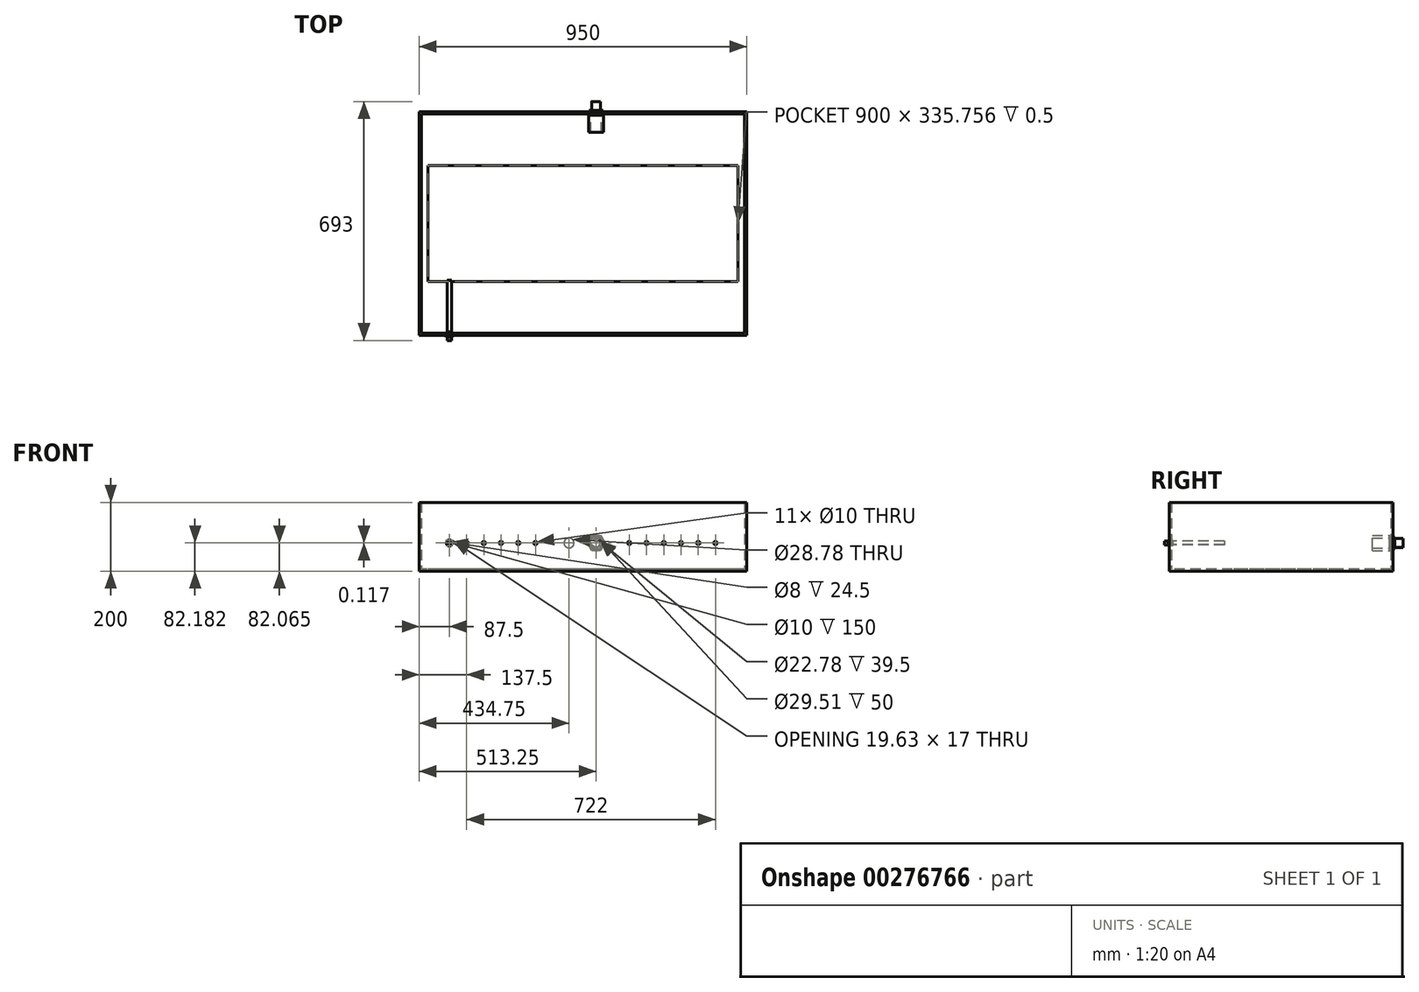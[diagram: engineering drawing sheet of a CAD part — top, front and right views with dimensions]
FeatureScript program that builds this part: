
annotation { "Feature Type Name" : "Feature", "Feature Type Description" : "" }
export const myFeature = defineFeature(function(context is Context, id is Id, definition is map)
    precondition{}
    {
        {
            var Q0;
            Q0=qCreatedBy(makeId("Top.planeOp"),FACE);
            var sketch = newSketch(context, id + "F0", { "sketchPlane" : qUnion([Q0])});
            skLineSegment(sketch, "E0.bottom", {"start": v(475, 325) * mm, "end": v(-475, 325) * mm});
            skLineSegment(sketch, "E0.top", {"start": v(475, -325) * mm, "end": v(-475, -325) * mm});
            skLineSegment(sketch, "E0.left", {"start": v(475, 325) * mm, "end": v(475, -325) * mm});
            skLineSegment(sketch, "E0.right", {"start": v(-475, 325) * mm, "end": v(-475, -325) * mm});
            skPoint(sketch, "E0.middle", {"position": v(0, 0) * mm});
            skSolve(sketch);
        }
        {
            var Q0;
            Q0=makeQuery(id+"F0.imprint","IMPRINT",FACE,{"disambiguationData":[TD([[makeQuery(id+"F0.imprint","IMPRINT",EDGE,{"derivedFrom":sQuery(id+"F0.wireOp",EDGE,"cca13281-c8a4-43dd-b4c7-58c42d9eb948.0")}),1.0]])]});
            var Q1;
            Q1=makeQuery(id+"F0.imprint","IMPRINT",FACE,{"disambiguationData":[TD([[makeQuery(id+"F0.imprint","IMPRINT",EDGE,{"derivedFrom":sQuery(id+"F0.wireOp",EDGE,"E0.bottom")}),1.0]])]});
            extrude(context, id + "F1", {"entities" : qUnion([Q0, Q1]), "depth" : 200 * mm});
        }
        {
            var Q0;
            Q0=makeQuery(id+"F1.opExtrude","CAP_FACE",FACE,{"disambiguationData":[OSD([sQuery(id+"F0.wireOp",EDGE,"E0.bottom"),sQuery(id+"F0.wireOp",EDGE,"E0.top"),sQuery(id+"F0.wireOp",EDGE,"E0.left"),sQuery(id+"F0.wireOp",EDGE,"E0.right")])],"isStart":false});
            shell(context, id + "F2", {"entities" : qUnion([Q0]), "thickness" : 2.5 * mm});
        }
        {
            var Q0;
            Q0=makeQuery(id+"F2.opShell","OFFSET_FACE",FACE,{"disambiguationData":[OSD([sQuery(id+"F0.wireOp",EDGE,"E0.bottom"),sQuery(id+"F0.wireOp",EDGE,"E0.top"),sQuery(id+"F0.wireOp",EDGE,"E0.left"),sQuery(id+"F0.wireOp",EDGE,"E0.right")])]});
            extrude(context, id + "F3", {"entities" : qUnion([Q0]), "depth" : 197.5 * mm});
        }
        {
            var Q0;
            Q0=makeQuery(id+"F3.opExtrude","CAP_FACE",FACE,{"disambiguationData":[OSD([sQuery(id+"F0.wireOp",EDGE,"E0.bottom"),sQuery(id+"F0.wireOp",EDGE,"E0.top"),sQuery(id+"F0.wireOp",EDGE,"E0.left"),sQuery(id+"F0.wireOp",EDGE,"E0.right")])],"isStart":false});
            shell(context, id + "F4", {"entities" : qUnion([Q0]), "thickness" : 4 * mm});
        }
        {
            var Q0;
            Q0=makeQuery(id+"F4.opShell","OFFSET_FACE",FACE,{"disambiguationData":[OSD([sQuery(id+"F0.wireOp",EDGE,"E0.bottom"),sQuery(id+"F0.wireOp",EDGE,"E0.top"),sQuery(id+"F0.wireOp",EDGE,"E0.left"),sQuery(id+"F0.wireOp",EDGE,"E0.right")])]});
            var sketch = newSketch(context, id + "F5", { "sketchPlane" : qUnion([Q0])});
            skLineSegment(sketch, "E1.bottom", {"start": v(450, 167.88) * mm, "end": v(-450, 167.88) * mm});
            skLineSegment(sketch, "E1.top", {"start": v(450, -167.88) * mm, "end": v(-450, -167.88) * mm});
            skLineSegment(sketch, "E1.left", {"start": v(450, 167.88) * mm, "end": v(450, -167.88) * mm});
            skLineSegment(sketch, "E1.right", {"start": v(-450, 167.88) * mm, "end": v(-450, -167.88) * mm});
            skPoint(sketch, "E1.middle", {"position": v(0, 0) * mm});
            skLineSegment(sketch, "E2.bottom", {"start": v(468.5, 318.5) * mm, "end": v(-468.5, 318.5) * mm});
            skLineSegment(sketch, "E2.top", {"start": v(468.5, -318.5) * mm, "end": v(-468.5, -318.5) * mm});
            skLineSegment(sketch, "E2.left", {"start": v(468.5, 318.5) * mm, "end": v(468.5, -318.5) * mm});
            skLineSegment(sketch, "E2.right", {"start": v(-468.5, 318.5) * mm, "end": v(-468.5, -318.5) * mm});
            skSolve(sketch);
        }
        {
            var Q0;
            Q0=makeQuery(id+"F5.imprint","IMPRINT",FACE,{"disambiguationData":[TD([[makeQuery(id+"F5.imprint","IMPRINT",EDGE,{"derivedFrom":sQuery(id+"F5.wireOp",EDGE,"E1.bottom")}),-1.0]])]});
            extrude(context, id + "F6", {"entities" : qUnion([Q0]), "operationType" : NewBodyOperationType.ADD, "depth" : 0.5 * mm});
        }
        {
            var Q0;
            Q0=makeQuery(id+"F1.opExtrude","SWEPT_FACE",FACE,{"disambiguationData":[OSD([sQuery(id+"F0.wireOp",EDGE,"E0.top")])]});
            var sketch = newSketch(context, id + "F7", { "sketchPlane" : qUnion([Q0])});
            skLineSegment(sketch, "E3.top", {"start": v(450, 6.5) * mm, "end": v(-450, 6.5) * mm, "construction": true});
            skPoint(sketch, "E3.middle", {"position": v(0, 100) * mm});
            skPoint(sketch, "E3.middle.positionSnap0", {"position": v(-475, 100) * mm});
            skPoint(sketch, "E3.centerSnap0", {"position": v(-475, 100) * mm});
            skLineSegment(sketch, "E4", {"start": v(-450, 6.5) * mm, "end": v(-450, 251.45) * mm, "construction": true});
            skLineSegment(sketch, "E5", {"start": v(-450, 251.45) * mm, "end": v(450, 251.45) * mm, "construction": true});
            skLineSegment(sketch, "E6", {"start": v(450, 251.45) * mm, "end": v(450, 6.5) * mm, "construction": true});
            skLineSegment(sketch, "E7", {"start": v(-450, 82.18) * mm, "end": v(-387.5, 82.18) * mm, "construction": true});
            skLineSegment(sketch, "E8", {"start": v(-387.5, 82.18) * mm, "end": v(-387.5, 6.5) * mm, "construction": true});
            skCircle(sketch, "E9", {"center": v(-387.5, 82.18) * mm, "radius": 5 * mm});
            skCircle(sketch, "E10.1.0.0", {"center": v(-337.5, 82.18) * mm, "radius": 5 * mm});
            skCircle(sketch, "E10.2.0.0", {"center": v(-287.5, 82.18) * mm, "radius": 5 * mm});
            skCircle(sketch, "E10.3.0.0", {"center": v(-237.5, 82.18) * mm, "radius": 5 * mm});
            skCircle(sketch, "E10.4.0.0", {"center": v(-187.5, 82.18) * mm, "radius": 5 * mm});
            skCircle(sketch, "E10.5.0.0", {"center": v(-137.5, 82.18) * mm, "radius": 5 * mm});
            skLineSegment(sketch, "E10.direction1", {"start": v(-387.5, 82.18) * mm, "end": v(-337.5, 82.18) * mm, "construction": true});
            skLineSegment(sketch, "E11", {"start": v(450, 82.07) * mm, "end": v(384.5, 82.07) * mm, "construction": true});
            skLineSegment(sketch, "E12", {"start": v(384.5, 82.07) * mm, "end": v(384.5, 6.5) * mm, "construction": true});
            skCircle(sketch, "E13", {"center": v(384.5, 82.07) * mm, "radius": 5 * mm});
            skCircle(sketch, "E14.1.0.0", {"center": v(334.5, 82.07) * mm, "radius": 5 * mm});
            skCircle(sketch, "E14.2.0.0", {"center": v(284.5, 82.07) * mm, "radius": 5 * mm});
            skCircle(sketch, "E14.3.0.0", {"center": v(234.5, 82.07) * mm, "radius": 5 * mm});
            skCircle(sketch, "E14.4.0.0", {"center": v(184.5, 82.07) * mm, "radius": 5 * mm});
            skCircle(sketch, "E14.5.0.0", {"center": v(134.5, 82.07) * mm, "radius": 5 * mm});
            skLineSegment(sketch, "E14.direction1", {"start": v(384.5, 82.07) * mm, "end": v(334.5, 82.07) * mm, "construction": true});
            skSolve(sketch);
        }
        {
            var Q0;
            Q0 = qSketchRegion(id + "F7", true);
            extrude(context, id + "F8", {"entities" : qUnion([Q0]), "operationType" : NewBodyOperationType.REMOVE, "oppositeDirection" : true, "depth" : 25 * mm});
        }
        {
            var Q0;
            Q0=makeQuery(id+"F1.opExtrude","SWEPT_FACE",FACE,{"disambiguationData":[OSD([sQuery(id+"F0.wireOp",EDGE,"E0.bottom")])]});
            var sketch = newSketch(context, id + "F9", { "sketchPlane" : qUnion([Q0])});
            skLineSegment(sketch, "E15", {"start": v(-450, 251.45) * mm, "end": v(-450, 6.5) * mm, "construction": true});
            skLineSegment(sketch, "E16", {"start": v(-450, 6.5) * mm, "end": v(450, 6.5) * mm, "construction": true});
            skLineSegment(sketch, "E17", {"start": v(450, 6.5) * mm, "end": v(450, 251.45) * mm, "construction": true});
            skLineSegment(sketch, "E18", {"start": v(450, 251.45) * mm, "end": v(-450, 251.45) * mm, "construction": true});
            skLineSegment(sketch, "E19", {"start": v(40.25, 6.5) * mm, "end": v(40.25, 82.07) * mm, "construction": true});
            skLineSegment(sketch, "E20", {"start": v(40.25, 82.07) * mm, "end": v(450, 82.07) * mm, "construction": true});
            skCircle(sketch, "E21", {"center": v(40.25, 82.07) * mm, "radius": 14.39 * mm});
            skCircle(sketch, "E22.1.0.0", {"center": v(-38.25, 82.07) * mm, "radius": 14.39 * mm});
            skLineSegment(sketch, "E22.direction1", {"start": v(40.25, 82.07) * mm, "end": v(-38.25, 82.07) * mm, "construction": true});
            skSolve(sketch);
        }
        {
            var Q0;
            Q0 = qSketchRegion(id + "F9", true);
            extrude(context, id + "F10", {"entities" : qUnion([Q0]), "operationType" : NewBodyOperationType.REMOVE, "oppositeDirection" : true, "depth" : 15 * mm});
        }
        {
            var Q0;
            Q0=makeQuery(id+"F1.opExtrude","SWEPT_FACE",FACE,{"disambiguationData":[OSD([sQuery(id+"F0.wireOp",EDGE,"E0.top")])]});
            var sketch = newSketch(context, id + "F11", { "sketchPlane" : qUnion([Q0])});
            skCircle(sketch, "E23", {"center": v(-387.5, 82.18) * mm, "radius": 4 * mm});
            skCircle(sketch, "E24.cCircle", {"center": v(-387.5, 82.18) * mm, "radius": 8.5 * mm, "construction": true});
            skLineSegment(sketch, "E24.0", {"start": v(-392.4, 90.68) * mm, "end": v(-382.6, 90.68) * mm});
            skLineSegment(sketch, "E24.1", {"start": v(-382.6, 90.68) * mm, "end": v(-377.69, 82.18) * mm});
            skLineSegment(sketch, "E24.2", {"start": v(-377.69, 82.18) * mm, "end": v(-382.6, 73.68) * mm});
            skLineSegment(sketch, "E24.3", {"start": v(-382.6, 73.68) * mm, "end": v(-392.4, 73.68) * mm});
            skLineSegment(sketch, "E24.4", {"start": v(-392.4, 73.68) * mm, "end": v(-397.31, 82.18) * mm});
            skLineSegment(sketch, "E24.5", {"start": v(-397.31, 82.18) * mm, "end": v(-392.4, 90.68) * mm});
            skPoint(sketch, "E24.0.midPoint", {"position": v(-387.5, 90.68) * mm});
            skSolve(sketch);
        }
        {
            var Q0;
            Q0 = qSketchRegion(id + "F11", true);
            extrude(context, id + "F12", {"entities" : qUnion([Q0]), "depth" : 4 * mm});
        }
        {
            var Q0;
            Q0=makeQuery(id+"F12.opExtrude","CAP_FACE",FACE,{"disambiguationData":[OSD([sQuery(id+"F11.wireOp",EDGE,"E23"),sQuery(id+"F11.wireOp",EDGE,"E24.0"),sQuery(id+"F11.wireOp",EDGE,"E24.1"),sQuery(id+"F11.wireOp",EDGE,"E24.2"),sQuery(id+"F11.wireOp",EDGE,"E24.3"),sQuery(id+"F11.wireOp",EDGE,"E24.4"),sQuery(id+"F11.wireOp",EDGE,"E24.5")])],"isStart":false});
            var sketch = newSketch(context, id + "F13", { "sketchPlane" : qUnion([Q0])});
            skCircle(sketch, "E25", {"center": v(-387.5, 82.18) * mm, "radius": 6 * mm});
            skCircle(sketch, "E26", {"center": v(-387.5, 82.18) * mm, "radius": 4 * mm});
            skSolve(sketch);
        }
        {
            var Q0;
            Q0 = qSketchRegion(id + "F13", true);
            extrude(context, id + "F14", {"entities" : qUnion([Q0]), "operationType" : NewBodyOperationType.ADD, "depth" : 10 * mm});
        }
        {
            var Q0;
            Q0=makeQuery(id+"F12.opExtrude","CAP_FACE",FACE,{"disambiguationData":[OSD([sQuery(id+"F11.wireOp",EDGE,"E23"),sQuery(id+"F11.wireOp",EDGE,"E24.0"),sQuery(id+"F11.wireOp",EDGE,"E24.1"),sQuery(id+"F11.wireOp",EDGE,"E24.2"),sQuery(id+"F11.wireOp",EDGE,"E24.3"),sQuery(id+"F11.wireOp",EDGE,"E24.4"),sQuery(id+"F11.wireOp",EDGE,"E24.5")])],"isStart":true});
            var sketch = newSketch(context, id + "F15", { "sketchPlane" : qUnion([Q0])});
            skCircle(sketch, "E27", {"center": v(387.5, 82.18) * mm, "radius": 5 * mm});
            skCircle(sketch, "E28", {"center": v(387.5, 82.18) * mm, "radius": 4 * mm});
            skSolve(sketch);
        }
        {
            var Q0;
            Q0 = qSketchRegion(id + "F15", true);
            extrude(context, id + "F16", {"entities" : qUnion([Q0]), "operationType" : NewBodyOperationType.ADD, "depth" : 6.5 * mm});
        }
        {
            var Q0;
            Q0=makeQuery(id+"F16.opExtrude","CAP_FACE",FACE,{"disambiguationData":[OSD([sQuery(id+"F15.wireOp",EDGE,"E27"),sQuery(id+"F15.wireOp",EDGE,"E28")])],"isStart":false});
            var sketch = newSketch(context, id + "F17", { "sketchPlane" : qUnion([Q0])});
            skCircle(sketch, "E29.cCircle", {"center": v(387.5, 82.18) * mm, "radius": 8.5 * mm, "construction": true});
            skLineSegment(sketch, "E29.0", {"start": v(382.6, 90.68) * mm, "end": v(392.4, 90.68) * mm});
            skLineSegment(sketch, "E29.1", {"start": v(392.4, 90.68) * mm, "end": v(397.31, 82.18) * mm});
            skLineSegment(sketch, "E29.2", {"start": v(397.31, 82.18) * mm, "end": v(392.4, 73.68) * mm});
            skLineSegment(sketch, "E29.3", {"start": v(392.4, 73.68) * mm, "end": v(382.6, 73.68) * mm});
            skLineSegment(sketch, "E29.4", {"start": v(382.6, 73.68) * mm, "end": v(377.69, 82.18) * mm});
            skLineSegment(sketch, "E29.5", {"start": v(377.69, 82.18) * mm, "end": v(382.6, 90.68) * mm});
            skPoint(sketch, "E29.0.midPoint", {"position": v(387.5, 90.68) * mm});
            skCircle(sketch, "E30", {"center": v(387.5, 82.18) * mm, "radius": 4 * mm});
            skSolve(sketch);
        }
        {
            var Q0;
            Q0=makeQuery(id+"F17.imprint","IMPRINT",FACE,{"disambiguationData":[TD([[makeQuery(id+"F17.imprint","IMPRINT",EDGE,{"derivedFrom":sQuery(id+"F17.wireOp",EDGE,"E30")}),1.0]])]});
            var Q1;
            Q1=makeQuery(id+"F17.imprint","IMPRINT",FACE,{"disambiguationData":[TD([[makeQuery(id+"F17.imprint","IMPRINT",EDGE,{"derivedFrom":sQuery(id+"F17.wireOp",EDGE,"E29.0")}),-1.0]])]});
            extrude(context, id + "F18", {"entities" : qUnion([Q0, Q1]), "operationType" : NewBodyOperationType.ADD, "depth" : 4 * mm});
        }
        {
            var Q0;
            Q0=makeQuery(id+"F18.opExtrude","CAP_FACE",FACE,{"disambiguationData":[OSD([sQuery(id+"F17.wireOp",EDGE,"E29.0"),sQuery(id+"F17.wireOp",EDGE,"E29.1"),sQuery(id+"F17.wireOp",EDGE,"E29.2"),sQuery(id+"F17.wireOp",EDGE,"E29.3"),sQuery(id+"F17.wireOp",EDGE,"E29.4"),sQuery(id+"F17.wireOp",EDGE,"E29.5"),sQuery(id+"F17.wireOp",EDGE,"E30")])],"isStart":false});
            var sketch = newSketch(context, id + "F19", { "sketchPlane" : qUnion([Q0])});
            skCircle(sketch, "E31", {"center": v(387.5, 82.18) * mm, "radius": 6 * mm});
            skCircle(sketch, "E32", {"center": v(387.5, 82.18) * mm, "radius": 5 * mm});
            skSolve(sketch);
        }
        {
            var Q0;
            Q0 = qSketchRegion(id + "F19", true);
            extrude(context, id + "F20", {"entities" : qUnion([Q0]), "operationType" : NewBodyOperationType.ADD, "depth" : 150 * mm});
        }
        {
            var Q0;
            Q0=makeQuery(id+"F1.opExtrude","SWEPT_FACE",FACE,{"disambiguationData":[OSD([sQuery(id+"F0.wireOp",EDGE,"E0.bottom")])]});
            var sketch = newSketch(context, id + "F21", { "sketchPlane" : qUnion([Q0])});
            skCircle(sketch, "E33", {"center": v(-38.25, 82.07) * mm, "radius": 11.39 * mm});
            skCircle(sketch, "E34.cCircle", {"center": v(-38.25, 82.07) * mm, "radius": 17.48 * mm, "construction": true});
            skLineSegment(sketch, "E34.0", {"start": v(-48.34, 99.55) * mm, "end": v(-28.16, 99.55) * mm});
            skLineSegment(sketch, "E34.1", {"start": v(-28.16, 99.55) * mm, "end": v(-18.07, 82.07) * mm});
            skLineSegment(sketch, "E34.2", {"start": v(-18.07, 82.07) * mm, "end": v(-28.16, 64.58) * mm});
            skLineSegment(sketch, "E34.3", {"start": v(-28.16, 64.58) * mm, "end": v(-48.34, 64.58) * mm});
            skLineSegment(sketch, "E34.4", {"start": v(-48.34, 64.58) * mm, "end": v(-58.43, 82.06) * mm});
            skLineSegment(sketch, "E34.5", {"start": v(-58.43, 82.06) * mm, "end": v(-48.34, 99.55) * mm});
            skPoint(sketch, "E34.0.midPoint", {"position": v(-38.25, 99.55) * mm});
            skSolve(sketch);
        }
        {
            var Q0;
            Q0 = qSketchRegion(id + "F21", true);
            extrude(context, id + "F22", {"entities" : qUnion([Q0]), "depth" : 4 * mm});
        }
        {
            var Q0;
            Q0=makeQuery(id+"F22.opExtrude","CAP_FACE",FACE,{"disambiguationData":[OSD([sQuery(id+"F21.wireOp",EDGE,"E33"),sQuery(id+"F21.wireOp",EDGE,"E34.0"),sQuery(id+"F21.wireOp",EDGE,"E34.1"),sQuery(id+"F21.wireOp",EDGE,"E34.2"),sQuery(id+"F21.wireOp",EDGE,"E34.3"),sQuery(id+"F21.wireOp",EDGE,"E34.4"),sQuery(id+"F21.wireOp",EDGE,"E34.5")])],"isStart":false});
            var sketch = newSketch(context, id + "F23", { "sketchPlane" : qUnion([Q0])});
            skCircle(sketch, "E35", {"center": v(-38.25, 82.07) * mm, "radius": 13.03 * mm});
            skCircle(sketch, "E36", {"center": v(-38.25, 82.07) * mm, "radius": 11.39 * mm});
            skSolve(sketch);
        }
        {
            var Q0;
            Q0 = qSketchRegion(id + "F23", true);
            extrude(context, id + "F24", {"entities" : qUnion([Q0]), "operationType" : NewBodyOperationType.ADD, "depth" : 25 * mm});
        }
        {
            var Q0;
            Q0=makeQuery(id+"F22.opExtrude","CAP_FACE",FACE,{"disambiguationData":[OSD([sQuery(id+"F21.wireOp",EDGE,"E33"),sQuery(id+"F21.wireOp",EDGE,"E34.0"),sQuery(id+"F21.wireOp",EDGE,"E34.1"),sQuery(id+"F21.wireOp",EDGE,"E34.2"),sQuery(id+"F21.wireOp",EDGE,"E34.3"),sQuery(id+"F21.wireOp",EDGE,"E34.4"),sQuery(id+"F21.wireOp",EDGE,"E34.5")])],"isStart":true});
            var sketch = newSketch(context, id + "F25", { "sketchPlane" : qUnion([Q0])});
            skCircle(sketch, "E37", {"center": v(38.25, 82.07) * mm, "radius": 14.39 * mm});
            skCircle(sketch, "E38", {"center": v(38.25, 82.07) * mm, "radius": 11.39 * mm});
            skSolve(sketch);
        }
        {
            var Q0;
            Q0 = qSketchRegion(id + "F25", true);
            extrude(context, id + "F26", {"entities" : qUnion([Q0]), "operationType" : NewBodyOperationType.ADD, "depth" : 6.5 * mm});
        }
        {
            var Q0;
            Q0=makeQuery(id+"F26.opExtrude","CAP_FACE",FACE,{"disambiguationData":[OSD([sQuery(id+"F25.wireOp",EDGE,"E37"),sQuery(id+"F25.wireOp",EDGE,"E38")])],"isStart":false});
            var sketch = newSketch(context, id + "F27", { "sketchPlane" : qUnion([Q0])});
            skCircle(sketch, "E39.cCircle", {"center": v(38.25, 82.07) * mm, "radius": 22 * mm, "construction": true});
            skLineSegment(sketch, "E39.0", {"start": v(25.55, 104.07) * mm, "end": v(50.95, 104.07) * mm});
            skLineSegment(sketch, "E39.1", {"start": v(50.95, 104.07) * mm, "end": v(63.66, 82.07) * mm});
            skLineSegment(sketch, "E39.2", {"start": v(63.66, 82.07) * mm, "end": v(50.95, 60.06) * mm});
            skLineSegment(sketch, "E39.3", {"start": v(50.95, 60.06) * mm, "end": v(25.55, 60.06) * mm});
            skLineSegment(sketch, "E39.4", {"start": v(25.55, 60.06) * mm, "end": v(12.84, 82.07) * mm});
            skLineSegment(sketch, "E39.5", {"start": v(12.84, 82.07) * mm, "end": v(25.55, 104.07) * mm});
            skPoint(sketch, "E39.0.midPoint", {"position": v(38.25, 104.07) * mm});
            skCircle(sketch, "E40", {"center": v(38.25, 82.07) * mm, "radius": 11.39 * mm});
            skSolve(sketch);
        }
        {
            var Q0;
            Q0 = qSketchRegion(id + "F27", true);
            extrude(context, id + "F28", {"entities" : qUnion([Q0]), "operationType" : NewBodyOperationType.ADD, "depth" : 4 * mm});
        }
        {
            var Q0;
            Q0=makeQuery(id+"F28.opExtrude","CAP_FACE",FACE,{"disambiguationData":[OSD([sQuery(id+"F27.wireOp",EDGE,"E39.0"),sQuery(id+"F27.wireOp",EDGE,"E39.1"),sQuery(id+"F27.wireOp",EDGE,"E39.2"),sQuery(id+"F27.wireOp",EDGE,"E39.3"),sQuery(id+"F27.wireOp",EDGE,"E39.4"),sQuery(id+"F27.wireOp",EDGE,"E39.5"),sQuery(id+"F27.wireOp",EDGE,"E40")])],"isStart":false});
            var sketch = newSketch(context, id + "F29", { "sketchPlane" : qUnion([Q0])});
            skCircle(sketch, "E41", {"center": v(38.25, 82.07) * mm, "radius": 22 * mm});
            skCircle(sketch, "E42", {"center": v(38.25, 82.07) * mm, "radius": 14.76 * mm});
            skSolve(sketch);
        }
        {
            var Q0;
            Q0 = qSketchRegion(id + "F29", true);
            extrude(context, id + "F30", {"entities" : qUnion([Q0]), "operationType" : NewBodyOperationType.ADD, "depth" : 50 * mm});
        }
    });
